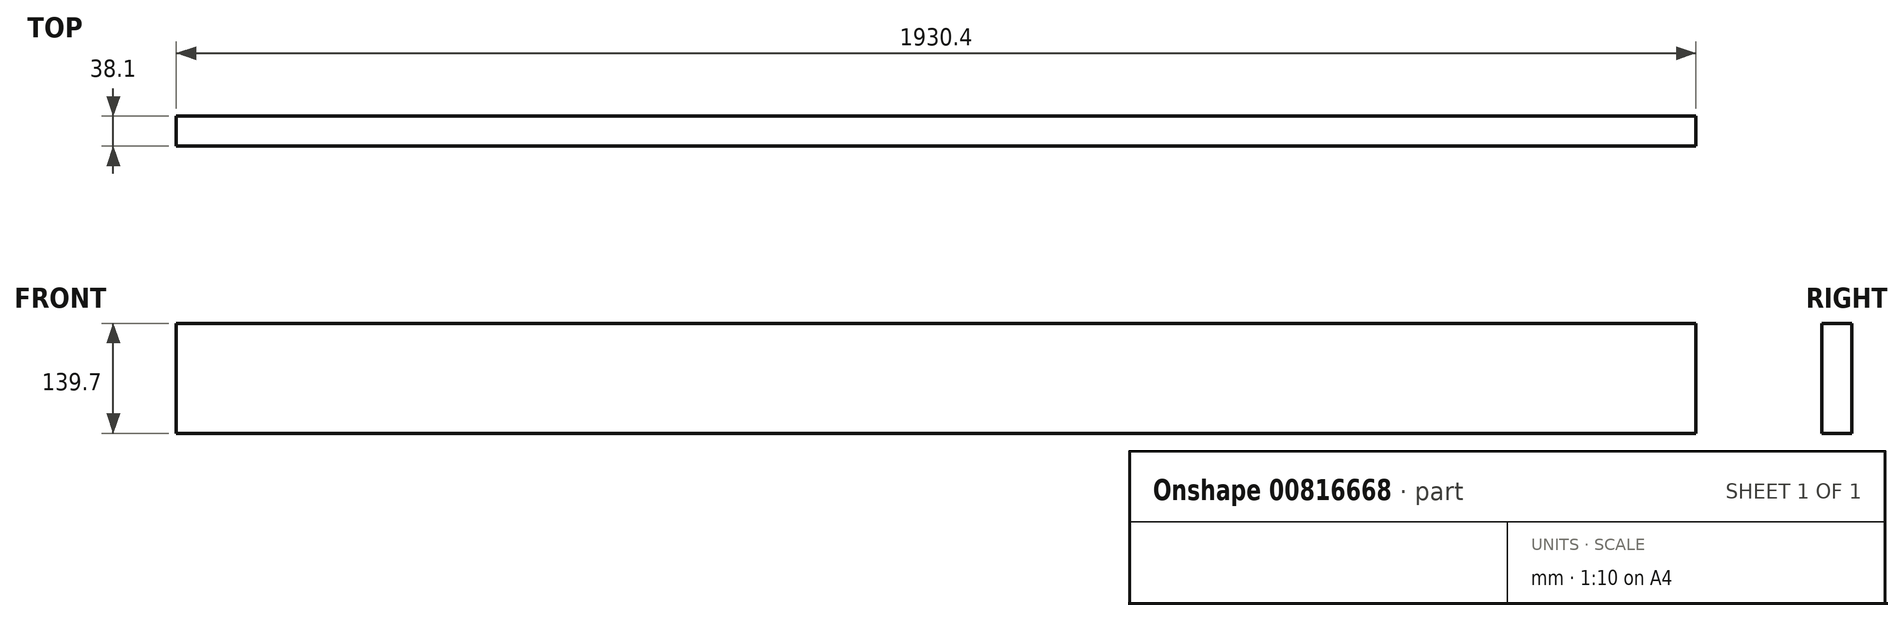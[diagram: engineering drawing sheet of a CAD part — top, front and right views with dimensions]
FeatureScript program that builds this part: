
annotation { "Feature Type Name" : "Feature", "Feature Type Description" : "" }
export const myFeature = defineFeature(function(context is Context, id is Id, definition is map)
    precondition{}
    {
        {
            var Q0;
            Q0=qCreatedBy(makeId("Top.planeOp"),FACE);
            var sketch = newSketch(context, id + "F0", { "sketchPlane" : qUnion([Q0])});
            skLineSegment(sketch, "E0.bottom", {"start": v(-951.03, -70.62) * mm, "end": v(979.37, -70.62) * mm});
            skLineSegment(sketch, "E0.top", {"start": v(-951.03, -108.72) * mm, "end": v(979.37, -108.72) * mm});
            skLineSegment(sketch, "E0.left", {"start": v(-951.03, -70.62) * mm, "end": v(-951.03, -108.72) * mm});
            skLineSegment(sketch, "E0.right", {"start": v(979.37, -70.62) * mm, "end": v(979.37, -108.72) * mm});
            skSolve(sketch);
        }
        {
            var Q0;
            Q0=makeQuery(id+"F0.imprint","IMPRINT",FACE,{"disambiguationData":[TD([[makeQuery(id+"F0.imprint","IMPRINT",EDGE,{"derivedFrom":sQuery(id+"F0.wireOp",EDGE,"E0.bottom")}),-1.0]])]});
            extrude(context, id + "F1", {"entities" : qUnion([Q0]), "depth" : 139.7 * mm, "offsetDistance" : 25.4 * mm});
        }
    });
